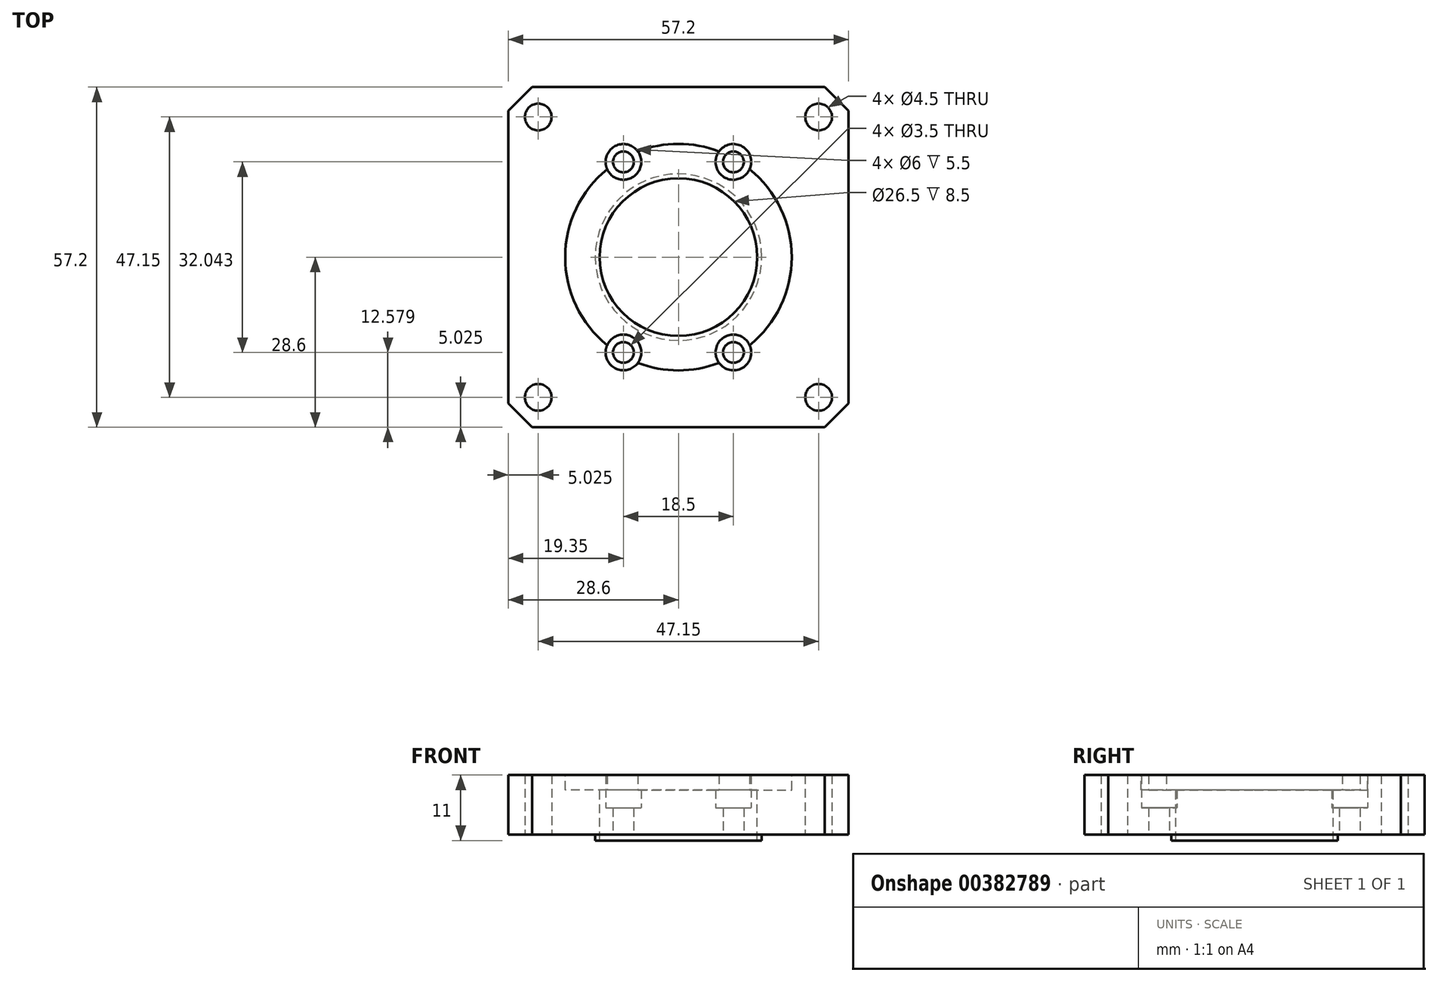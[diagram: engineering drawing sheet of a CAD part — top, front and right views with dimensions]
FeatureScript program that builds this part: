
annotation { "Feature Type Name" : "Feature", "Feature Type Description" : "" }
export const myFeature = defineFeature(function(context is Context, id is Id, definition is map)
    precondition{}
    {
        {
            var Q0;
            Q0=qCreatedBy(makeId("Top.planeOp"),FACE);
            var sketch = newSketch(context, id + "F0", { "sketchPlane" : qUnion([Q0])});
            skLineSegment(sketch, "E0.bottom", {"start": v(28.6, -28.6) * mm, "end": v(-28.6, -28.6) * mm});
            skLineSegment(sketch, "E0.top", {"start": v(28.6, 28.6) * mm, "end": v(-28.6, 28.6) * mm});
            skLineSegment(sketch, "E0.left", {"start": v(28.6, -28.6) * mm, "end": v(28.6, 28.6) * mm});
            skLineSegment(sketch, "E0.right", {"start": v(-28.6, -28.6) * mm, "end": v(-28.6, 28.6) * mm});
            skPoint(sketch, "E0.middle", {"position": v(0, 0) * mm});
            skSolve(sketch);
        }
        {
            var Q0;
            Q0=makeQuery(id+"F0.imprint","IMPRINT",FACE,{"disambiguationData":[TD([[makeQuery(id+"F0.imprint","IMPRINT",EDGE,{"derivedFrom":sQuery(id+"F0.wireOp",EDGE,"E0.bottom")}),-1.0]])]});
            extrude(context, id + "F1", {"entities" : qUnion([Q0]), "depth" : 10 * mm, "offsetDistance" : 25 * mm});
        }
        {
            var Q0;
            Q0=makeQuery(id+"F1.opExtrude","SWEPT_EDGE",EDGE,{"disambiguationData":[OSD([sQuery(id+"F0.wireOp",EDGE,"E0.top"),sQuery(id+"F0.wireOp",EDGE,"E0.right")])]});
            var Q1;
            Q1=makeQuery(id+"F1.opExtrude","SWEPT_EDGE",EDGE,{"disambiguationData":[OSD([sQuery(id+"F0.wireOp",EDGE,"E0.top"),sQuery(id+"F0.wireOp",EDGE,"E0.left")])]});
            var Q2;
            Q2=makeQuery(id+"F1.opExtrude","SWEPT_EDGE",EDGE,{"disambiguationData":[OSD([sQuery(id+"F0.wireOp",EDGE,"E0.bottom"),sQuery(id+"F0.wireOp",EDGE,"E0.left")])]});
            var Q3;
            Q3=makeQuery(id+"F1.opExtrude","SWEPT_EDGE",EDGE,{"disambiguationData":[OSD([sQuery(id+"F0.wireOp",EDGE,"E0.bottom"),sQuery(id+"F0.wireOp",EDGE,"E0.right")])]});
            chamfer(context, id + "F2", {"entities" : qUnion([Q0, Q1, Q2, Q3]), "width" : 4 * mm, "tangentPropagation" : true});
        }
        {
            var Q0;
            Q0=makeQuery(id+"F1.opExtrude","CAP_FACE",FACE,{"disambiguationData":[OSD([sQuery(id+"F0.wireOp",EDGE,"E0.bottom"),sQuery(id+"F0.wireOp",EDGE,"E0.top"),sQuery(id+"F0.wireOp",EDGE,"E0.left"),sQuery(id+"F0.wireOp",EDGE,"E0.right")])],"isStart":false});
            var sketch = newSketch(context, id + "F3", { "sketchPlane" : qUnion([Q0])});
            skCircle(sketch, "E1", {"center": v(0, 0) * mm, "radius": 19.05 * mm});
            skSolve(sketch);
        }
        {
            var Q0;
            Q0=makeQuery(id+"F3.imprint","IMPRINT",FACE,{"disambiguationData":[TD([[makeQuery(id+"F3.imprint","IMPRINT",EDGE,{"derivedFrom":sQuery(id+"F3.wireOp",EDGE,"E1")}),1.0]])]});
            extrude(context, id + "F4", {"entities" : qUnion([Q0]), "operationType" : NewBodyOperationType.REMOVE, "oppositeDirection" : true, "depth" : 2.5 * mm, "offsetDistance" : 25 * mm});
        }
        {
            var Q0;
            Q0=makeQuery(id+"F1.opExtrude","CAP_FACE",FACE,{"disambiguationData":[OSD([sQuery(id+"F0.wireOp",EDGE,"E0.bottom"),sQuery(id+"F0.wireOp",EDGE,"E0.top"),sQuery(id+"F0.wireOp",EDGE,"E0.left"),sQuery(id+"F0.wireOp",EDGE,"E0.right")])],"isStart":true});
            var sketch = newSketch(context, id + "F5", { "sketchPlane" : qUnion([Q0])});
            skCircle(sketch, "E2", {"center": v(0, 0) * mm, "radius": 14 * mm});
            skSolve(sketch);
        }
        {
            var Q0;
            Q0=makeQuery(id+"F5.imprint","IMPRINT",FACE,{"disambiguationData":[TD([[makeQuery(id+"F5.imprint","IMPRINT",EDGE,{"derivedFrom":sQuery(id+"F5.wireOp",EDGE,"E2")}),1.0]])]});
            extrude(context, id + "F6", {"entities" : qUnion([Q0]), "operationType" : NewBodyOperationType.ADD, "depth" : 1 * mm, "offsetDistance" : 25 * mm});
        }
        {
            var Q0;
            Q0=makeQuery(id+"F4.boolean.opBoolean","COPY",FACE,{"derivedFrom":makeQuery(id+"F4.opExtrude","CAP_FACE",FACE,{"disambiguationData":[OSD([sQuery(id+"F3.wireOp",EDGE,"E1")])],"isStart":false})});
            var sketch = newSketch(context, id + "F7", { "sketchPlane" : qUnion([Q0])});
            skCircle(sketch, "E3", {"center": v(0, 0) * mm, "radius": 13.25 * mm});
            skSolve(sketch);
        }
        {
            var Q0;
            Q0=makeQuery(id+"F7.imprint","IMPRINT",FACE,{"disambiguationData":[TD([[makeQuery(id+"F7.imprint","IMPRINT",EDGE,{"derivedFrom":sQuery(id+"F7.wireOp",EDGE,"E3")}),1.0]])]});
            extrude(context, id + "F8", {"entities" : qUnion([Q0]), "operationType" : NewBodyOperationType.REMOVE, "endBound" : BoundingType.THROUGH_ALL, "oppositeDirection" : true, "depth" : 25 * mm, "offsetDistance" : 25 * mm});
        }
        {
            var Q0;
            Q0=makeQuery(id+"F1.opExtrude","CAP_FACE",FACE,{"disambiguationData":[OSD([sQuery(id+"F0.wireOp",EDGE,"E0.bottom"),sQuery(id+"F0.wireOp",EDGE,"E0.top"),sQuery(id+"F0.wireOp",EDGE,"E0.left"),sQuery(id+"F0.wireOp",EDGE,"E0.right")])],"isStart":false});
            var sketch = newSketch(context, id + "F9", { "sketchPlane" : qUnion([Q0])});
            skPoint(sketch, "E4", {"position": v(-23.57, 23.57) * mm});
            skLineSegment(sketch, "E5", {"start": v(0, 0) * mm, "end": v(-23.57, 23.57) * mm});
            skPoint(sketch, "E6.1.0", {"position": v(-23.57, -23.57) * mm});
            skPoint(sketch, "E6.2.0", {"position": v(23.57, -23.57) * mm});
            skPoint(sketch, "E6.3.0", {"position": v(23.57, 23.57) * mm});
            skPoint(sketch, "E6.center", {"position": v(0, 0) * mm});
            skSolve(sketch);
        }
        {
            var Q0;
            Q0=sQuery(id+"F9.wireOp",VERTEX,"E4");
            var Q1;
            Q1=sQuery(id+"F9.wireOp",VERTEX,"E6.3.0");
            var Q2;
            Q2=sQuery(id+"F9.wireOp",VERTEX,"E6.2.0");
            var Q3;
            Q3=sQuery(id+"F9.wireOp",VERTEX,"E6.1.0");
            var Q4;
            Q4=makeQuery(id+"F1.opExtrude","SWEPT_BODY",BODY,{"disambiguationData":[OSD([sQuery(id+"F0.wireOp",EDGE,"E0.bottom"),sQuery(id+"F0.wireOp",EDGE,"E0.top"),sQuery(id+"F0.wireOp",EDGE,"E0.left"),sQuery(id+"F0.wireOp",EDGE,"E0.right")])]});
            hole(context, id + "F10", {"style" : HoleStyle.SIMPLE, "endStyle" : HoleEndStyle.THROUGH, "standardTappedOrClearance" : lookupTablePath({ "fit" : "Normal", "standard" : "ISO", "size" : "M4", "type" : "Clearance" }), "standardBlindInLast" : lookupTablePath({ "fit" : "Normal", "standard" : "ISO", "engagement" : "75%", "pitch" : "0.7 mm", "size" : "M4", "type" : "Clearance & tapped" }), "holeDiameter" : 4.5 * mm, "majorDiameter" : 5 * mm, "isTappedThrough" : true, "tappedDepth" : 9 * mm, "tapClearance" : 3, "locations" : qUnion([Q0, Q1, Q2, Q3]), "scope" : qUnion([Q4]), "startStyle" : HoleStartStyle.PART});
        }
        {
            var Q0;
            Q0=makeQuery(id+"F1.opExtrude","CAP_FACE",FACE,{"disambiguationData":[OSD([sQuery(id+"F0.wireOp",EDGE,"E0.bottom"),sQuery(id+"F0.wireOp",EDGE,"E0.top"),sQuery(id+"F0.wireOp",EDGE,"E0.left"),sQuery(id+"F0.wireOp",EDGE,"E0.right")])],"isStart":false});
            var sketch = newSketch(context, id + "F11", { "sketchPlane" : qUnion([Q0])});
            skPoint(sketch, "E7", {"position": v(-9.25, -16.02) * mm});
            skLineSegment(sketch, "E8", {"start": v(0, 0) * mm, "end": v(-9.25, -16.02) * mm});
            skPoint(sketch, "E9.MirrorP", {"position": v(9.25, -16.02) * mm});
            skPoint(sketch, "E10.MirrorP", {"position": v(9.25, 16.02) * mm});
            skPoint(sketch, "E11.MirrorP", {"position": v(-9.25, 16.02) * mm});
            skSolve(sketch);
        }
        {
            var Q0;
            Q0=sQuery(id+"F11.wireOp",VERTEX,"E11.MirrorP");
            var Q1;
            Q1=sQuery(id+"F11.wireOp",VERTEX,"E10.MirrorP");
            var Q2;
            Q2=sQuery(id+"F11.wireOp",VERTEX,"E9.MirrorP");
            var Q3;
            Q3=sQuery(id+"F11.wireOp",VERTEX,"E7");
            var Q4;
            Q4=makeQuery(id+"F1.opExtrude","SWEPT_BODY",BODY,{"disambiguationData":[OSD([sQuery(id+"F0.wireOp",EDGE,"E0.bottom"),sQuery(id+"F0.wireOp",EDGE,"E0.top"),sQuery(id+"F0.wireOp",EDGE,"E0.left"),sQuery(id+"F0.wireOp",EDGE,"E0.right")])]});
            hole(context, id + "F12", {"style" : HoleStyle.C_BORE, "endStyle" : HoleEndStyle.THROUGH, "holeDiameter" : 3.5 * mm, "cBoreDiameter" : 6 * mm, "cBoreDepth" : 3 * mm, "majorDiameter" : 5 * mm, "isTappedThrough" : true, "tappedDepth" : 9 * mm, "tapClearance" : 3, "locations" : qUnion([Q0, Q1, Q2, Q3]), "scope" : qUnion([Q4]), "startStyle" : HoleStartStyle.PART});
        }
    });
